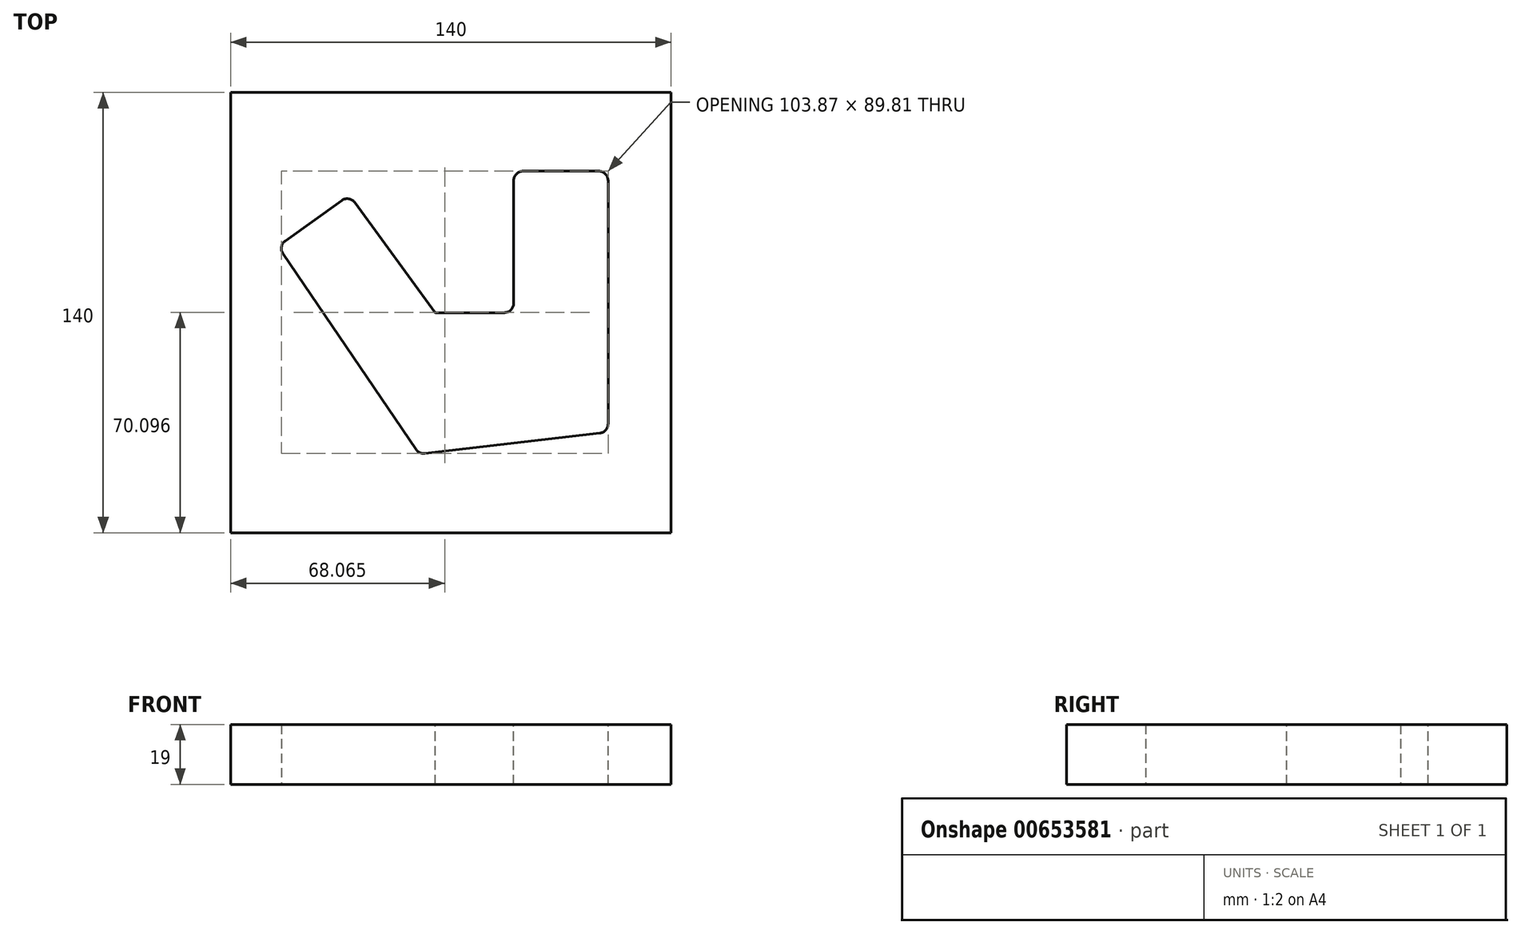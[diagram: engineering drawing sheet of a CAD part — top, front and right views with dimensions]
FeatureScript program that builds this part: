
annotation { "Feature Type Name" : "Feature", "Feature Type Description" : "" }
export const myFeature = defineFeature(function(context is Context, id is Id, definition is map)
    precondition{}
    {
        {
            var Q0;
            Q0=qCreatedBy(makeId("Top.planeOp"),FACE);
            var sketch = newSketch(context, id + "F0", { "sketchPlane" : qUnion([Q0])});
            skLineSegment(sketch, "E0.bottom", {"start": v(70, 70) * mm, "end": v(-70, 70) * mm});
            skLineSegment(sketch, "E0.top", {"start": v(70, -70) * mm, "end": v(-70, -70) * mm});
            skLineSegment(sketch, "E0.left", {"start": v(70, 70) * mm, "end": v(70, -70) * mm});
            skLineSegment(sketch, "E0.right", {"start": v(-70, 70) * mm, "end": v(-70, -70) * mm});
            skPoint(sketch, "E0.middle", {"position": v(0, 0) * mm});
            skSolve(sketch);
        }
        {
            var Q0;
            Q0=makeQuery(id+"F0.imprint","IMPRINT",FACE,{"disambiguationData":[TD([[makeQuery(id+"F0.imprint","IMPRINT",EDGE,{"derivedFrom":sQuery(id+"F0.wireOp",EDGE,"E0.bottom")}),1.0]])]});
            extrude(context, id + "F1", {"entities" : qUnion([Q0]), "depth" : 19 * mm, "offsetDistance" : 25 * mm});
        }
        {
            var Q0;
            Q0=makeQuery(id+"F1.opExtrude","CAP_FACE",FACE,{"disambiguationData":[OSD([sQuery(id+"F0.wireOp",EDGE,"E0.bottom"),sQuery(id+"F0.wireOp",EDGE,"E0.top"),sQuery(id+"F0.wireOp",EDGE,"E0.left"),sQuery(id+"F0.wireOp",EDGE,"E0.right")])],"isStart":false});
            var sketch = newSketch(context, id + "F2", { "sketchPlane" : qUnion([Q0])});
            skPoint(sketch, "E1", {"position": v(50, -38) * mm});
            skPoint(sketch, "E2", {"position": v(50, 45) * mm});
            skPoint(sketch, "E3", {"position": v(20, 45) * mm});
            skPoint(sketch, "E4", {"position": v(-55, 21.14) * mm});
            skPoint(sketch, "E5", {"position": v(-10, -45) * mm});
            skPoint(sketch, "E6", {"position": v(-32.2, 37.4) * mm});
            skPoint(sketch, "E7", {"position": v(20, 0) * mm});
            skLineSegment(sketch, "E8", {"start": v(0, 0) * mm, "end": v(20, 0) * mm});
            skLineSegment(sketch, "E9", {"start": v(20, 0) * mm, "end": v(20, 45) * mm});
            skLineSegment(sketch, "E10", {"start": v(20, 45) * mm, "end": v(50, 45) * mm});
            skLineSegment(sketch, "E11", {"start": v(50, 45) * mm, "end": v(50, -38) * mm});
            skLineSegment(sketch, "E12", {"start": v(50, -38) * mm, "end": v(-10, -45) * mm});
            skLineSegment(sketch, "E13", {"start": v(-10, -45) * mm, "end": v(-55, 21.14) * mm});
            skLineSegment(sketch, "E14", {"start": v(-55, 21.14) * mm, "end": v(-32.2, 37.4) * mm});
            skPoint(sketch, "E15", {"position": v(-5, 0) * mm});
            skLineSegment(sketch, "E16", {"start": v(-32.2, 37.4) * mm, "end": v(-5, 0) * mm});
            skLineSegment(sketch, "E17", {"start": v(0, 0) * mm, "end": v(-5, 0) * mm});
            skSolve(sketch);
        }
        {
            var Q0;
            Q0=makeQuery(id+"F2.imprint","IMPRINT",FACE,{"disambiguationData":[TD([[makeQuery(id+"F2.imprint","IMPRINT",EDGE,{"derivedFrom":sQuery(id+"F2.wireOp",EDGE,"wDgV1IdW-ptEa-eQMs-FUAb-OkshIPqnGdG5")}),-1.0]])]});
            var Q1;
            Q1=makeQuery(id+"F2.imprint","IMPRINT",FACE,{"disambiguationData":[TD([[makeQuery(id+"F2.imprint","IMPRINT",EDGE,{"derivedFrom":sQuery(id+"F2.wireOp",EDGE,"E8")}),-1.0]])]});
            extrude(context, id + "F3", {"entities" : qUnion([Q0, Q1]), "operationType" : NewBodyOperationType.REMOVE, "oppositeDirection" : true, "depth" : 20 * mm, "offsetDistance" : 25 * mm});
        }
        {
            var Q0;
            Q0=makeQuery(id+"F3.boolean.opBoolean","COPY",EDGE,{"derivedFrom":makeQuery(id+"F3.opExtrude","SWEPT_EDGE",EDGE,{"disambiguationData":[OSD([sQuery(id+"F2.wireOp",EDGE,"E11"),sQuery(id+"F2.wireOp",EDGE,"E12")])]})});
            var Q1;
            Q1=makeQuery(id+"F3.boolean.opBoolean","COPY",EDGE,{"derivedFrom":makeQuery(id+"F3.opExtrude","SWEPT_EDGE",EDGE,{"disambiguationData":[OSD([sQuery(id+"F2.wireOp",EDGE,"E10"),sQuery(id+"F2.wireOp",EDGE,"E11")])]})});
            var Q2;
            Q2=makeQuery(id+"F3.boolean.opBoolean","COPY",EDGE,{"derivedFrom":makeQuery(id+"F3.opExtrude","SWEPT_EDGE",EDGE,{"disambiguationData":[OSD([sQuery(id+"F2.wireOp",EDGE,"E9"),sQuery(id+"F2.wireOp",EDGE,"E10")])]})});
            var Q3;
            Q3=makeQuery(id+"F3.boolean.opBoolean","COPY",EDGE,{"derivedFrom":makeQuery(id+"F3.opExtrude","SWEPT_EDGE",EDGE,{"disambiguationData":[OSD([sQuery(id+"F2.wireOp",EDGE,"E8"),sQuery(id+"F2.wireOp",EDGE,"E9")])]})});
            var Q4;
            Q4=makeQuery(id+"F3.boolean.opBoolean","COPY",EDGE,{"derivedFrom":makeQuery(id+"F3.opExtrude","SWEPT_EDGE",EDGE,{"disambiguationData":[OSD([sQuery(id+"F2.wireOp",EDGE,"wDgV1IdW-ptEa-eQMs-FUAb-OkshIPqnGdG5"),sQuery(id+"F2.wireOp",EDGE,"E8")])]})});
            var Q5;
            Q5=makeQuery(id+"F3.boolean.opBoolean","COPY",EDGE,{"derivedFrom":makeQuery(id+"F3.opExtrude","SWEPT_EDGE",EDGE,{"disambiguationData":[OSD([sQuery(id+"F2.wireOp",EDGE,"wDgV1IdW-ptEa-eQMs-FUAb-OkshIPqnGdG5"),sQuery(id+"F2.wireOp",EDGE,"E14")])]})});
            var Q6;
            Q6=makeQuery(id+"F3.boolean.opBoolean","COPY",EDGE,{"derivedFrom":makeQuery(id+"F3.opExtrude","SWEPT_EDGE",EDGE,{"disambiguationData":[OSD([sQuery(id+"F2.wireOp",EDGE,"E13"),sQuery(id+"F2.wireOp",EDGE,"E14")])]})});
            var Q7;
            Q7=makeQuery(id+"F3.boolean.opBoolean","COPY",EDGE,{"derivedFrom":makeQuery(id+"F3.opExtrude","SWEPT_EDGE",EDGE,{"disambiguationData":[OSD([sQuery(id+"F2.wireOp",EDGE,"E12"),sQuery(id+"F2.wireOp",EDGE,"E13")])]})});
            fillet(context, id + "F4", {"entities" : qUnion([Q0, Q1, Q2, Q3, Q4, Q5, Q6, Q7]), "radius" : 3 * mm, "tangentPropagation" : true, "allowEdgeOverflow" : false});
        }
    });
